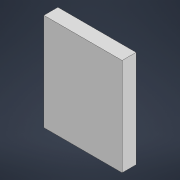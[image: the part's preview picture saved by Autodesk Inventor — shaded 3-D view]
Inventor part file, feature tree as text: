
AUTODESK INVENTOR PART (.ipt)
format: ipt  version: 2022 (Build 260153000, 153)  size: 83,968 bytes
history: native  units: mm
features: other x1, extrude x1, sketch x1
ambient origin geometry x8: Origin, YZ Plane, XZ Plane, XY Plane, X Axis, Y Axis, Z Axis, Center Point
bodies: Body1 (feature_tree)
feature tree (3):
  other  "Твердое тело1"
  extrude  "Выдавливание1"  Depth=246.0mm
  sketch  "Эскиз1"
